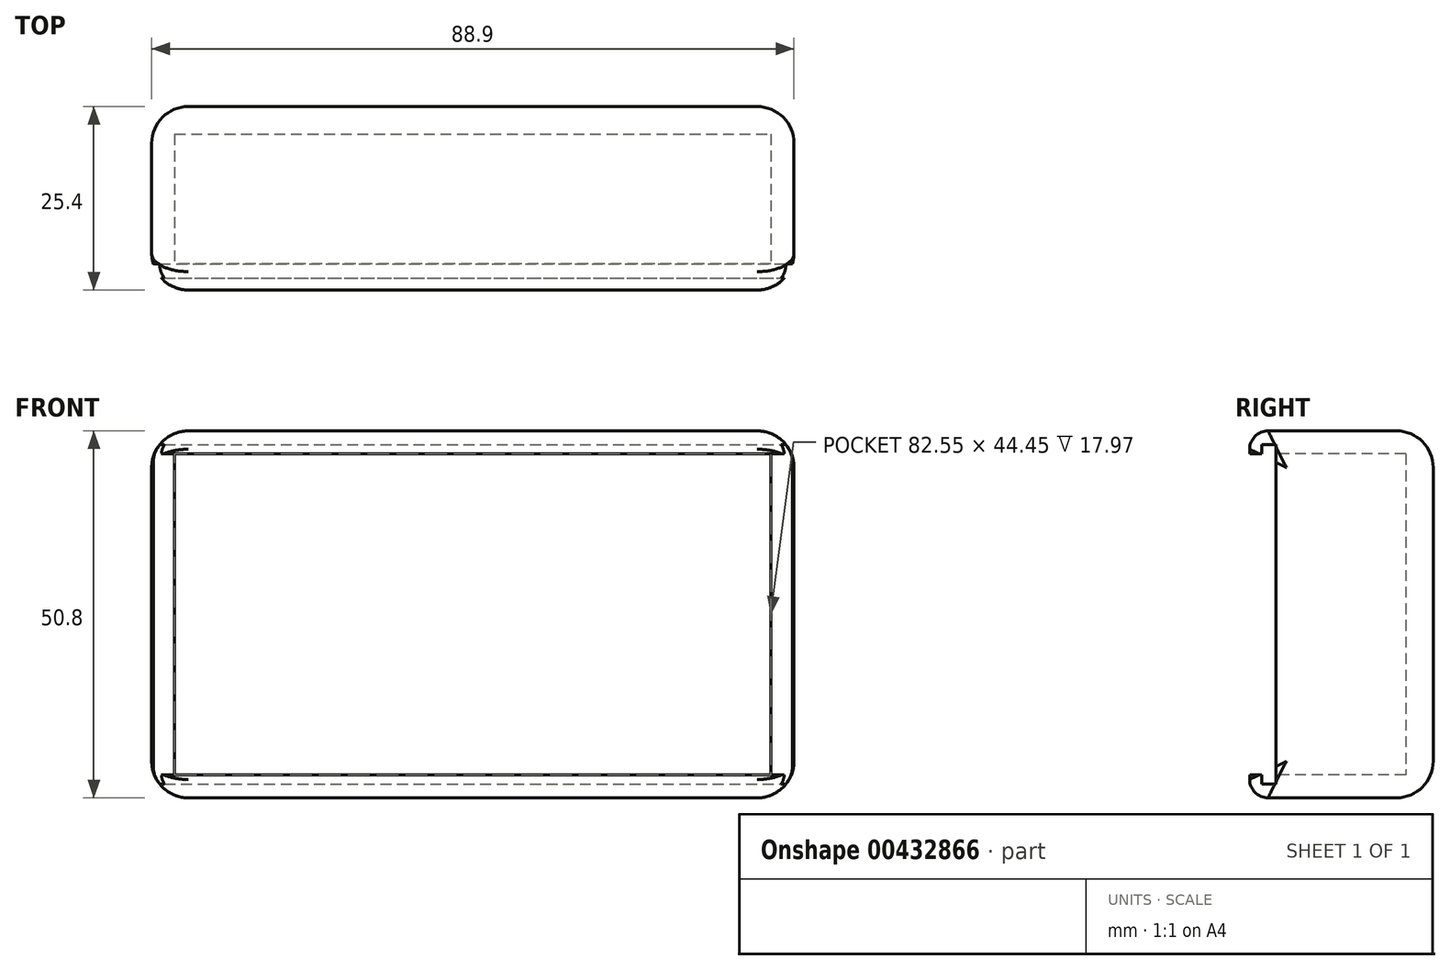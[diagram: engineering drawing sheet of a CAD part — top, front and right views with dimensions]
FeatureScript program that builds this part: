
annotation { "Feature Type Name" : "Feature", "Feature Type Description" : "" }
export const myFeature = defineFeature(function(context is Context, id is Id, definition is map)
    precondition{}
    {
        {
            var Q0;
            Q0=qCreatedBy(makeId("Front.planeOp"),FACE);
            var sketch = newSketch(context, id + "F0", { "sketchPlane" : qUnion([Q0])});
            skLineSegment(sketch, "E0.bottom", {"start": v(0, 0) * mm, "end": v(88.9, 0) * mm});
            skLineSegment(sketch, "E0.top", {"start": v(0, 50.8) * mm, "end": v(88.9, 50.8) * mm});
            skLineSegment(sketch, "E0.left", {"start": v(0, 0) * mm, "end": v(0, 50.8) * mm});
            skLineSegment(sketch, "E0.right", {"start": v(88.9, 0) * mm, "end": v(88.9, 50.8) * mm});
            skSolve(sketch);
        }
        {
            var Q0;
            Q0=makeQuery(id+"F0.imprint","IMPRINT",FACE,{"disambiguationData":[TD([[makeQuery(id+"F0.imprint","IMPRINT",EDGE,{"derivedFrom":sQuery(id+"F0.wireOp",EDGE,"E0.bottom")}),1.0]])]});
            extrude(context, id + "F1", {"entities" : qUnion([Q0]), "depth" : 25.4 * mm});
        }
        {
            var Q0;
            Q0=makeQuery(id+"F1.opExtrude","SWEPT_FACE",FACE,{"disambiguationData":[OSD([sQuery(id+"F0.wireOp",EDGE,"E0.right")])]});
            var sketch = newSketch(context, id + "F2", { "sketchPlane" : qUnion([Q0])});
            skLineSegment(sketch, "E1", {"start": v(-25.4, 0) * mm, "end": v(-25.4, 3.18) * mm});
            skLineSegment(sketch, "E2", {"start": v(-25.4, 3.18) * mm, "end": v(-23.75, 3.18) * mm});
            skLineSegment(sketch, "E3", {"start": v(-23.75, 3.17) * mm, "end": v(-23.75, 1.9) * mm});
            skLineSegment(sketch, "E4", {"start": v(-23.75, 1.9) * mm, "end": v(-21.78, 1.9) * mm});
            skLineSegment(sketch, "E5", {"start": v(-21.78, 48.9) * mm, "end": v(-23.75, 48.9) * mm});
            skLineSegment(sketch, "E6", {"start": v(-23.75, 48.9) * mm, "end": v(-23.75, 47.62) * mm});
            skLineSegment(sketch, "E7", {"start": v(-23.75, 47.62) * mm, "end": v(-25.4, 47.62) * mm});
            skLineSegment(sketch, "E8", {"start": v(-21.78, 1.9) * mm, "end": v(-21.78, 48.9) * mm});
            skLineSegment(sketch, "E9", {"start": v(-25.4, 47.62) * mm, "end": v(-25.4, 50.8) * mm});
            skSolve(sketch);
        }
        {
            var Q0;
            {var subQ0=sQuery(id+"F2.wireOp",EDGE,"E2");Q0=makeQuery(id+"F2.imprint","IMPRINT",FACE,{"disambiguationData":[TD([[makeQuery(id+"F2.imprint","IMPRINT",EDGE,{"derivedFrom":subQ0}),1.0]])]});}
            extrude(context, id + "F3", {"entities" : qUnion([Q0]), "operationType" : NewBodyOperationType.REMOVE, "endBound" : BoundingType.THROUGH_ALL, "oppositeDirection" : true, "depth" : 25.4 * mm});
        }
        {
            var Q0;
            {var subQ0=sQuery(id+"F0.wireOp",EDGE,"E0.top");var subQ1=sQuery(id+"F0.wireOp",EDGE,"E0.left");var subQ2=sQuery(id+"F0.wireOp",EDGE,"E0.right");Q0=makeQuery(id+"F3.boolean.opBoolean","SPLIT",FACE,{"disambiguationData":[TD([makeQuery(id+"F1.opExtrude","SWEPT_FACE",FACE,{"disambiguationData":[OSD([subQ0])]})])],"derivedFrom":makeQuery(id+"F1.opExtrude","CAP_FACE",FACE,{"disambiguationData":[OSD([sQuery(id+"F0.wireOp",EDGE,"E0.bottom"),subQ0,subQ1,subQ2])],"isStart":false})});}
            var sketch = newSketch(context, id + "F4", { "sketchPlane" : qUnion([Q0])});
            skLineSegment(sketch, "E10.bottom", {"start": v(3.17, 47.63) * mm, "end": v(85.73, 47.63) * mm});
            skLineSegment(sketch, "E10.top", {"start": v(3.17, 3.18) * mm, "end": v(85.73, 3.18) * mm});
            skLineSegment(sketch, "E10.left", {"start": v(3.17, 47.63) * mm, "end": v(3.18, 3.18) * mm});
            skLineSegment(sketch, "E10.right", {"start": v(85.73, 47.63) * mm, "end": v(85.73, 3.18) * mm});
            skSolve(sketch);
        }
        {
            var Q0;
            Q0=makeQuery(id+"F4.imprint","IMPRINT",FACE,{"disambiguationData":[TD([[makeQuery(id+"F4.imprint","IMPRINT",EDGE,{"derivedFrom":sQuery(id+"F4.wireOp",EDGE,"E10.bottom")}),-1.0]])]});
            extrude(context, id + "F5", {"entities" : qUnion([Q0]), "operationType" : NewBodyOperationType.REMOVE, "oppositeDirection" : true, "depth" : 21.59 * mm});
        }
        {
            var Q0;
            Q0=makeQuery(id+"F1.opExtrude","CAP_EDGE",EDGE,{"disambiguationData":[OSD([sQuery(id+"F0.wireOp",EDGE,"E0.top")])],"isStart":false});
            var Q1;
            Q1=makeQuery(id+"F1.opExtrude","CAP_EDGE",EDGE,{"disambiguationData":[OSD([sQuery(id+"F0.wireOp",EDGE,"E0.bottom")])],"isStart":false});
            fillet(context, id + "F6", {"entities" : qUnion([Q0, Q1]), "radius" : 2.54 * mm, "tangentPropagation" : true, "allowEdgeOverflow" : false});
        }
        {
            var Q0;
            Q0=makeQuery(id+"F1.opExtrude","CAP_EDGE",EDGE,{"disambiguationData":[OSD([sQuery(id+"F0.wireOp",EDGE,"E0.left")])],"isStart":true});
            var Q1;
            Q1=makeQuery(id+"F1.opExtrude","CAP_EDGE",EDGE,{"disambiguationData":[OSD([sQuery(id+"F0.wireOp",EDGE,"E0.top")])],"isStart":true});
            var Q2;
            Q2=makeQuery(id+"F1.opExtrude","CAP_EDGE",EDGE,{"disambiguationData":[OSD([sQuery(id+"F0.wireOp",EDGE,"E0.right")])],"isStart":true});
            var Q3;
            Q3=makeQuery(id+"F1.opExtrude","CAP_EDGE",EDGE,{"disambiguationData":[OSD([sQuery(id+"F0.wireOp",EDGE,"E0.bottom")])],"isStart":true});
            var Q4;
            Q4=makeQuery(id+"F1.opExtrude","SWEPT_EDGE",EDGE,{"disambiguationData":[OSD([sQuery(id+"F0.wireOp",EDGE,"E0.bottom"),sQuery(id+"F0.wireOp",EDGE,"E0.right")])]});
            var Q5;
            Q5=makeQuery(id+"F1.opExtrude","SWEPT_EDGE",EDGE,{"disambiguationData":[OSD([sQuery(id+"F0.wireOp",EDGE,"E0.top"),sQuery(id+"F0.wireOp",EDGE,"E0.right")])]});
            var Q6;
            Q6=makeQuery(id+"F1.opExtrude","SWEPT_EDGE",EDGE,{"disambiguationData":[OSD([sQuery(id+"F0.wireOp",EDGE,"E0.bottom"),sQuery(id+"F0.wireOp",EDGE,"E0.left")])]});
            var Q7;
            Q7=makeQuery(id+"F1.opExtrude","SWEPT_EDGE",EDGE,{"disambiguationData":[OSD([sQuery(id+"F0.wireOp",EDGE,"E0.top"),sQuery(id+"F0.wireOp",EDGE,"E0.left")])]});
            fillet(context, id + "F7", {"entities" : qUnion([Q0, Q1, Q2, Q3, Q4, Q5, Q6, Q7]), "radius" : 5.08 * mm, "tangentPropagation" : true, "allowEdgeOverflow" : false});
        }
    });
